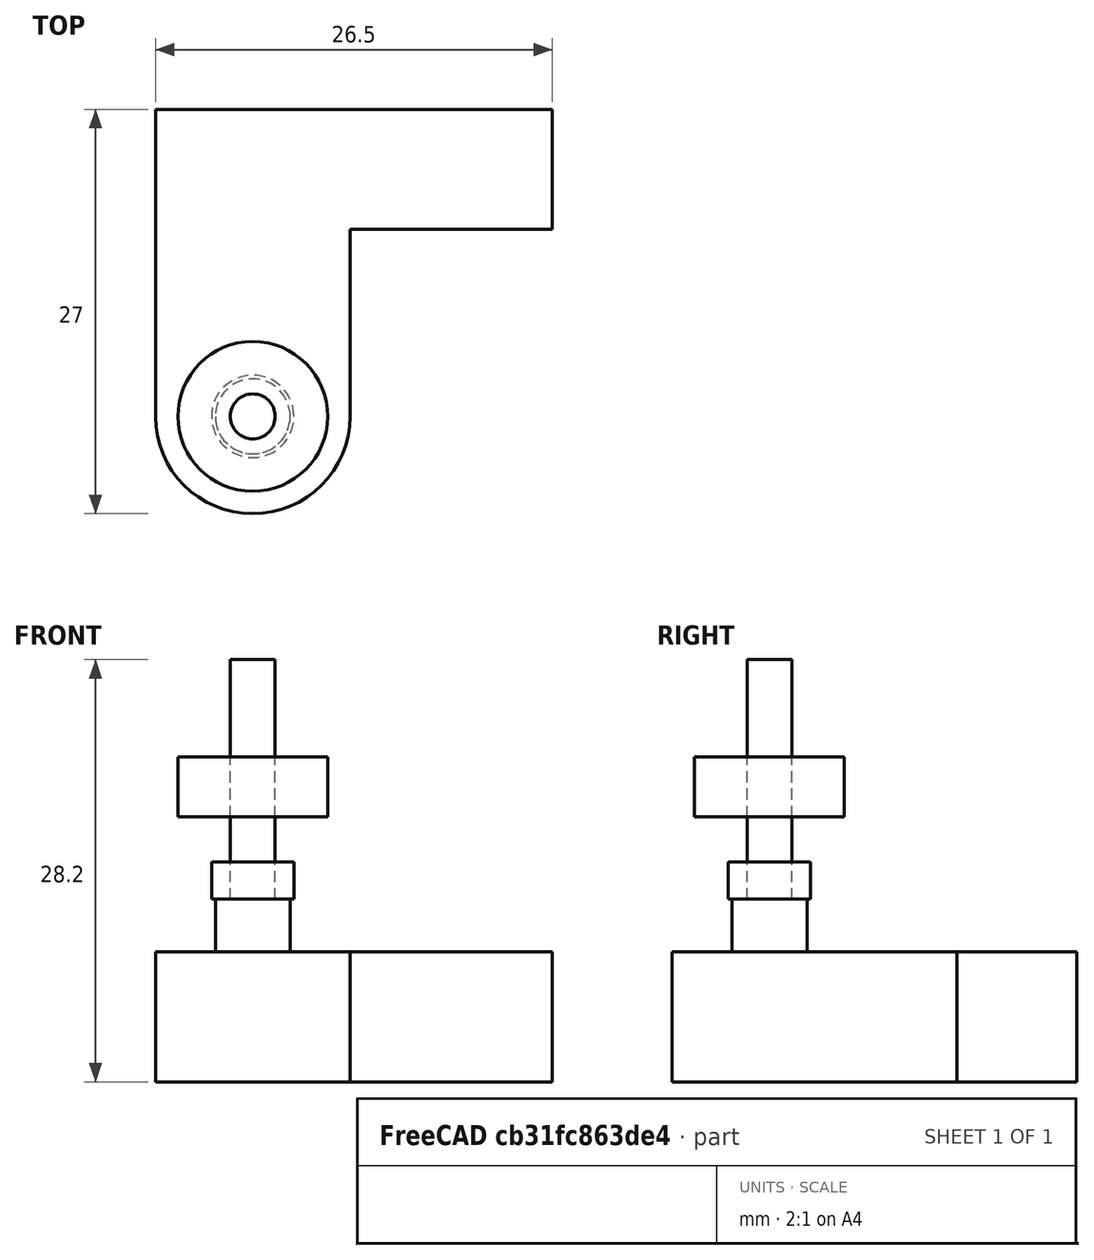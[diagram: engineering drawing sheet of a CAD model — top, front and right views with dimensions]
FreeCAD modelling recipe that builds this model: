
FCSTD DOCUMENT  (FreeCAD 0.18.3R)
Label: motorised-clamp
License: All rights reserved
LicenseURL: http://en.wikipedia.org/wiki/All_rights_reserved
objects: Part::Cylinder×6, Part::Box×2, Part::MultiFuse×1
note: 9 computed .brp shape members not serialized (recipe doc carries the construction recipe); baked Part::Feature solids carry a one-line shape summary decoded from their .brp

FEATURE [Part::Cylinder] Cylinder
  Angle = 360
  AttacherType = Attacher::AttachEngine3D
  Height = 16
  Placement = pos=(0,0,3.5) rot=(0,0,1;0rad)
  Radius = 1.5
FEATURE [Part::Cylinder] Cylinder001
  Angle = 360
  AttacherType = Attacher::AttachEngine3D
  Height = 2.5
  Placement = pos=(0,0,3.5) rot=(0,0,1;0rad)
  Radius = 2.75
FEATURE [Part::Cylinder] Cylinder002
  Angle = 360
  AttacherType = Attacher::AttachEngine3D
  Height = 3.5
  Radius = 2.5
FEATURE [Part::Cylinder] Cylinder003
  Angle = 360
  AttacherType = Attacher::AttachEngine3D
  Height = 8.7
  Placement = pos=(0,0,-8.7) rot=(0,0,1;0rad)
  Radius = 6.5
FEATURE [Part::Box] Box  label="Cube"
  AttacherType = Attacher::AttachEngine3D
  Height = 8.7
  Length = 13
  Placement = pos=(-6.5,0,-8.7) rot=(0,0,1;0rad)
  Width = 20.5
FEATURE [Part::Box] Box001  label="Cube001"
  AttacherType = Attacher::AttachEngine3D
  Height = 8.7
  Length = 25
  Placement = pos=(-5,12.5,-8.7) rot=(0,0,1;0rad)
  Width = 8
FEATURE [Part::MultiFuse] Fusion  label="motor"
  Shapes = -> [Cylinder002,Cylinder003,Box001,Box]
FEATURE [Part::Cylinder] Cylinder004  label="motor-shaft-1"
  Angle = 360
  AttacherType = Attacher::AttachEngine3D
  Height = 3.5
  Radius = 2.5
FEATURE [Part::Cylinder] Cylinder005  label="bearing"
  Angle = 360
  AttacherType = Attacher::AttachEngine3D
  Height = 4
  Placement = pos=(0,0,9) rot=(0,0,1;0rad)
  Radius = 5
